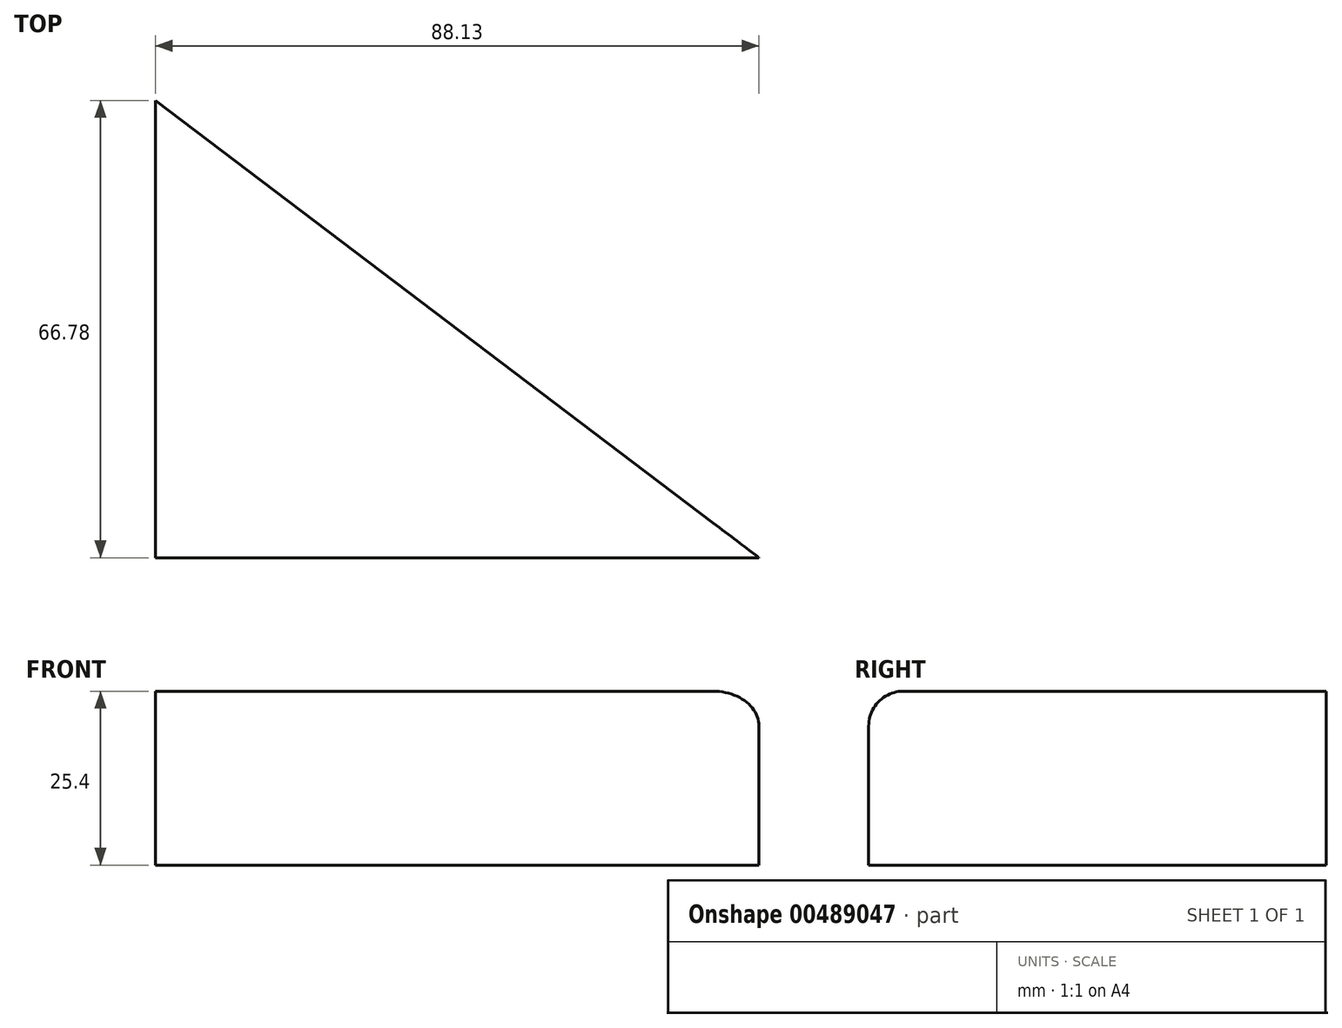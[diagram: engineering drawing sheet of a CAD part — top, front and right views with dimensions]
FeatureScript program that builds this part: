
annotation { "Feature Type Name" : "Feature", "Feature Type Description" : "" }
export const myFeature = defineFeature(function(context is Context, id is Id, definition is map)
    precondition{}
    {
        {
            var Q0;
            Q0=qCreatedBy(makeId("Top.planeOp"),FACE);
            var sketch = newSketch(context, id + "F0", { "sketchPlane" : qUnion([Q0])});
            skLineSegment(sketch, "E0", {"start": v(-37.6, 40) * mm, "end": v(-37.6, -26.77) * mm});
            skLineSegment(sketch, "E1", {"start": v(-37.6, -26.77) * mm, "end": v(50.53, -26.77) * mm});
            skLineSegment(sketch, "E2", {"start": v(50.53, -26.77) * mm, "end": v(-37.6, 40) * mm});
            skSolve(sketch);
        }
        {
            var Q0;
            Q0 = qSketchRegion(id + "F0", true);
            extrude(context, id + "F1", {"entities" : qUnion([Q0]), "depth" : 25.4 * mm});
        }
        {
            var Q0;
            Q0=makeQuery(id+"F1.opExtrude","CAP_EDGE",EDGE,{"disambiguationData":[OSD([sQuery(id+"F0.wireOp",EDGE,"E1")])],"isStart":false});
            fillet(context, id + "F2", {"entities" : qUnion([Q0]), "radius" : 5.08 * mm, "tangentPropagation" : true, "allowEdgeOverflow" : false});
        }
    });
